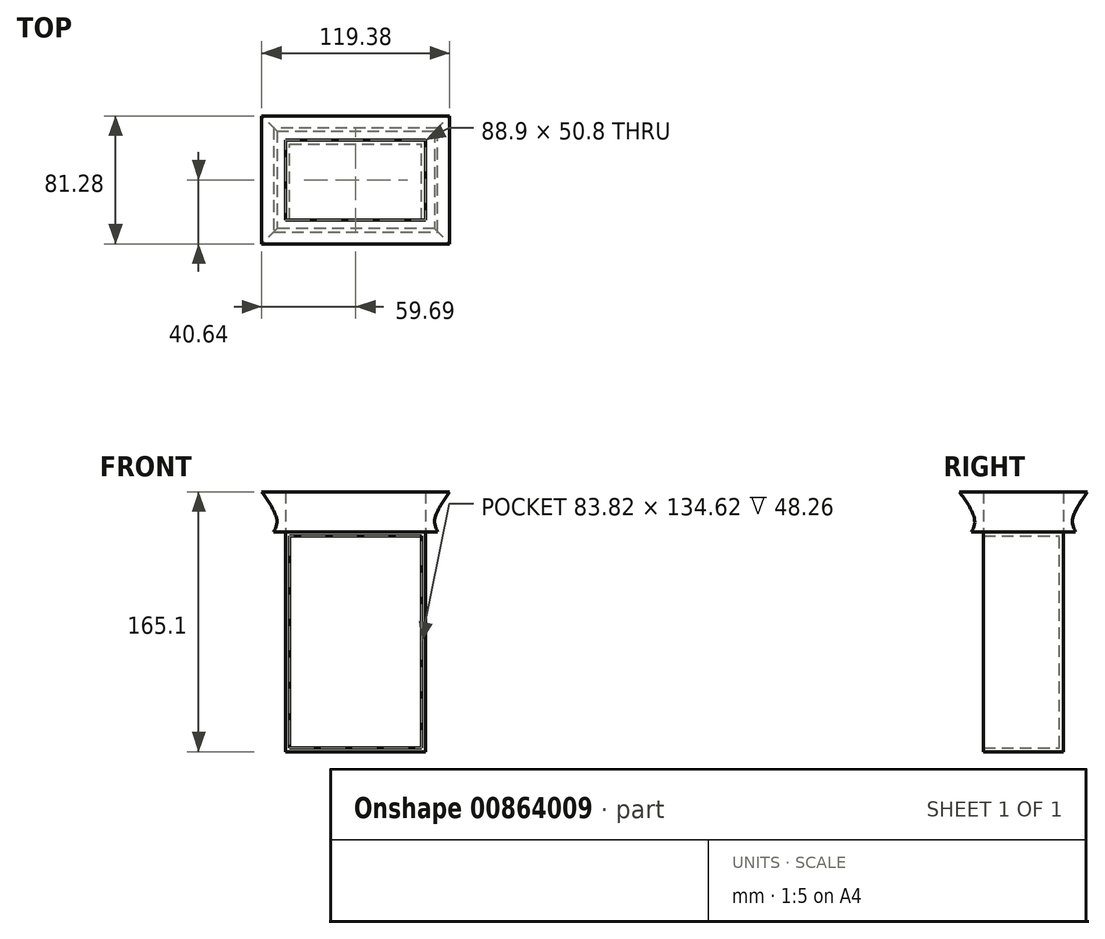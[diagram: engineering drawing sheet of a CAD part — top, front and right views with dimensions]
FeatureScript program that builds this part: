
annotation { "Feature Type Name" : "Feature", "Feature Type Description" : "" }
export const myFeature = defineFeature(function(context is Context, id is Id, definition is map)
    precondition{}
    {
        {
            var Q0;
            Q0=qCreatedBy(makeId("Front.planeOp"),FACE);
            var sketch = newSketch(context, id + "F0", { "sketchPlane" : qUnion([Q0])});
            skLineSegment(sketch, "E0.bottom", {"start": v(0, 0) * mm, "end": v(88.9, 0) * mm});
            skLineSegment(sketch, "E0.top", {"start": v(0, 139.7) * mm, "end": v(88.9, 139.7) * mm});
            skLineSegment(sketch, "E0.left", {"start": v(0, 0) * mm, "end": v(0, 139.7) * mm});
            skLineSegment(sketch, "E0.right", {"start": v(88.9, 0) * mm, "end": v(88.9, 139.7) * mm});
            skSolve(sketch);
        }
        {
            var Q0;
            Q0=makeQuery(id+"F0.imprint","IMPRINT",FACE,{"disambiguationData":[TD([[makeQuery(id+"F0.imprint","IMPRINT",EDGE,{"derivedFrom":sQuery(id+"F0.wireOp",EDGE,"E0.bottom")}),1.0]])]});
            extrude(context, id + "F1", {"entities" : qUnion([Q0]), "depth" : 50.8 * mm, "offsetDistance" : 25.4 * mm});
        }
        {
            var Q0;
            Q0=makeQuery(id+"F1.opExtrude","CAP_FACE",FACE,{"disambiguationData":[OSD([sQuery(id+"F0.wireOp",EDGE,"E0.bottom"),sQuery(id+"F0.wireOp",EDGE,"E0.top"),sQuery(id+"F0.wireOp",EDGE,"E0.left"),sQuery(id+"F0.wireOp",EDGE,"E0.right")])],"isStart":false});
            shell(context, id + "F2", {"entities" : qUnion([Q0]), "thickness" : 2.54 * mm});
        }
        {
            var Q0;
            Q0=makeQuery(id+"F1.opExtrude","SWEPT_FACE",FACE,{"disambiguationData":[OSD([sQuery(id+"F0.wireOp",EDGE,"E0.top")])]});
            var sketch = newSketch(context, id + "F3", { "sketchPlane" : qUnion([Q0])});
            skLineSegment(sketch, "E1", {"start": v(88.9, 0) * mm, "end": v(88.9, -50.8) * mm});
            skLineSegment(sketch, "E2", {"start": v(88.9, -50.8) * mm, "end": v(0, -50.8) * mm});
            skLineSegment(sketch, "E3", {"start": v(0, -50.8) * mm, "end": v(0, 0) * mm});
            skLineSegment(sketch, "E4", {"start": v(0, 0) * mm, "end": v(88.9, 0) * mm});
            skSolve(sketch);
        }
        {
            var Q0;
            Q0=makeQuery(id+"F1.opExtrude","CAP_FACE",FACE,{"disambiguationData":[OSD([sQuery(id+"F0.wireOp",EDGE,"E0.bottom"),sQuery(id+"F0.wireOp",EDGE,"E0.top"),sQuery(id+"F0.wireOp",EDGE,"E0.left"),sQuery(id+"F0.wireOp",EDGE,"E0.right")])],"isStart":true});
            var sketch = newSketch(context, id + "F4", { "sketchPlane" : qUnion([Q0])});
            skLineSegment(sketch, "E5", {"start": v(0, 139.7) * mm, "end": v(0, 165.1) * mm});
            skLineSegment(sketch, "E6", {"start": v(0, 165.1) * mm, "end": v(15.24, 165.1) * mm});
            skLineSegment(sketch, "E7", {"start": v(0, 139.7) * mm, "end": v(7.62, 139.7) * mm});
            skFitSpline(sketch, "E8", {"points": [v(7.62, 139.7) * mm, v(5.7, 147.28) * mm, v(15.24, 165.1) * mm], "startDerivative": vector(-8.95, 18) * mm, "endDerivative": vector(21.8, 31.72) * mm});
            skSolve(sketch);
        }
        {
            var Q0;
            Q0=makeQuery(id+"F4.imprint","IMPRINT",FACE,{"disambiguationData":[TD([[makeQuery(id+"F4.imprint","IMPRINT",EDGE,{"derivedFrom":sQuery(id+"F4.wireOp",EDGE,"E5")}),-1.0]])]});
            var Q1;
            Q1=sQuery(id+"F3.wireOp",EDGE,"E4");
            var Q2;
            Q2=sQuery(id+"F3.wireOp",EDGE,"E3");
            var Q3;
            Q3=sQuery(id+"F3.wireOp",EDGE,"E2");
            var Q4;
            Q4=sQuery(id+"F3.wireOp",EDGE,"E1");
            sweep(context, id + "F5", {"profiles" : qUnion([Q0]), "path" : qUnion([Q1, Q2, Q3, Q4])});
        }
        {
            var Q0;
            Q0=makeQuery(id+"F1.opExtrude","SWEPT_FACE",FACE,{"disambiguationData":[OSD([sQuery(id+"F0.wireOp",EDGE,"E0.top")])]});
            extrude(context, id + "F6", {"entities" : qUnion([Q0]), "depth" : 25.4 * mm, "offsetDistance" : 25.4 * mm});
        }
    });
